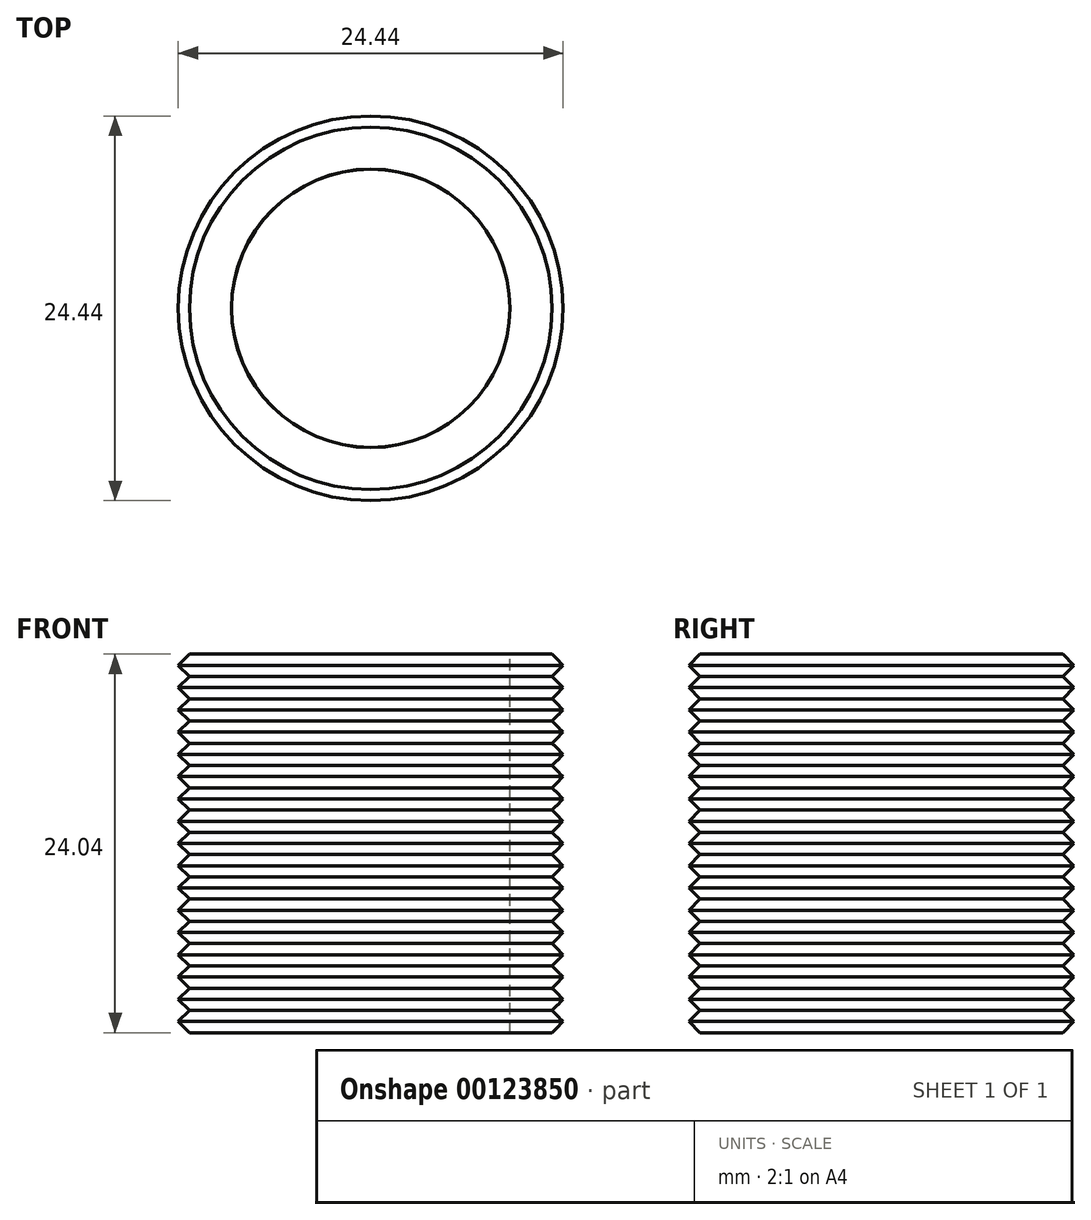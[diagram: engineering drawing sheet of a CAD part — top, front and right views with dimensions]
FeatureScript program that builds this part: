
annotation { "Feature Type Name" : "Feature", "Feature Type Description" : "" }
export const myFeature = defineFeature(function(context is Context, id is Id, definition is map)
    precondition{}
    {
        {
            var Q0;
            Q0=qCreatedBy(makeId("Front.planeOp"),FACE);
            var sketch = newSketch(context, id + "F0", { "sketchPlane" : qUnion([Q0])});
            skLineSegment(sketch, "E0.bottom", {"start": v(-8.84, 0) * mm, "end": v(-11.51, 0) * mm});
            skLineSegment(sketch, "E0.left", {"start": v(-8.84, 0) * mm, "end": v(-8.84, -24.04) * mm});
            skLineSegment(sketch, "E1", {"start": v(-11.51, 0) * mm, "end": v(-12.22, -0.7) * mm});
            skLineSegment(sketch, "E2", {"start": v(-12.22, -0.7) * mm, "end": v(-11.51, -1.41) * mm});
            skLineSegment(sketch, "E3", {"start": v(-11.51, -1.41) * mm, "end": v(-12.22, -2.12) * mm});
            skLineSegment(sketch, "E4", {"start": v(-12.22, -2.12) * mm, "end": v(-11.51, -2.83) * mm});
            skLineSegment(sketch, "E5", {"start": v(-11.51, -2.83) * mm, "end": v(-12.22, -3.54) * mm});
            skLineSegment(sketch, "E6", {"start": v(-12.22, -3.54) * mm, "end": v(-11.51, -4.24) * mm});
            skLineSegment(sketch, "E7", {"start": v(-11.51, -4.24) * mm, "end": v(-12.22, -4.95) * mm});
            skLineSegment(sketch, "E8", {"start": v(-12.22, -4.95) * mm, "end": v(-11.51, -5.66) * mm});
            skLineSegment(sketch, "E9", {"start": v(-11.51, -5.66) * mm, "end": v(-12.22, -6.36) * mm});
            skLineSegment(sketch, "E10", {"start": v(-12.22, -6.36) * mm, "end": v(-11.51, -7.07) * mm});
            skLineSegment(sketch, "E11", {"start": v(-11.51, -7.07) * mm, "end": v(-12.22, -7.78) * mm});
            skLineSegment(sketch, "E12", {"start": v(-12.22, -7.78) * mm, "end": v(-11.51, -8.49) * mm});
            skLineSegment(sketch, "E13", {"start": v(-11.51, -8.49) * mm, "end": v(-12.22, -9.2) * mm});
            skLineSegment(sketch, "E14", {"start": v(-12.22, -9.2) * mm, "end": v(-11.51, -9.9) * mm});
            skLineSegment(sketch, "E15", {"start": v(-11.51, -9.9) * mm, "end": v(-12.22, -10.6) * mm});
            skLineSegment(sketch, "E16", {"start": v(-12.22, -10.6) * mm, "end": v(-11.51, -11.31) * mm});
            skLineSegment(sketch, "E17", {"start": v(-11.51, -11.31) * mm, "end": v(-12.22, -12.02) * mm});
            skLineSegment(sketch, "E18", {"start": v(-12.22, -12.02) * mm, "end": v(-11.51, -12.73) * mm});
            skLineSegment(sketch, "E19", {"start": v(-11.51, -12.73) * mm, "end": v(-12.22, -13.44) * mm});
            skLineSegment(sketch, "E20", {"start": v(-12.22, -13.44) * mm, "end": v(-11.51, -14.14) * mm});
            skLineSegment(sketch, "E21", {"start": v(-11.51, -14.14) * mm, "end": v(-12.22, -14.85) * mm});
            skLineSegment(sketch, "E22", {"start": v(-12.22, -14.85) * mm, "end": v(-11.51, -15.56) * mm});
            skLineSegment(sketch, "E23", {"start": v(-11.51, -15.56) * mm, "end": v(-12.22, -16.26) * mm});
            skLineSegment(sketch, "E24", {"start": v(-12.22, -16.26) * mm, "end": v(-11.51, -16.97) * mm});
            skLineSegment(sketch, "E25", {"start": v(-11.51, -16.97) * mm, "end": v(-12.22, -17.68) * mm});
            skLineSegment(sketch, "E26", {"start": v(-12.22, -17.68) * mm, "end": v(-11.51, -18.38) * mm});
            skLineSegment(sketch, "E27", {"start": v(-11.51, -18.38) * mm, "end": v(-12.22, -19.1) * mm});
            skLineSegment(sketch, "E28", {"start": v(-12.22, -19.1) * mm, "end": v(-11.51, -19.8) * mm});
            skLineSegment(sketch, "E29", {"start": v(-11.51, -19.8) * mm, "end": v(-12.22, -20.5) * mm});
            skLineSegment(sketch, "E30", {"start": v(-12.22, -20.5) * mm, "end": v(-11.51, -21.21) * mm});
            skLineSegment(sketch, "E31", {"start": v(-11.51, -21.21) * mm, "end": v(-12.22, -21.92) * mm});
            skLineSegment(sketch, "E32", {"start": v(-12.22, -21.92) * mm, "end": v(-11.51, -22.63) * mm});
            skLineSegment(sketch, "E33", {"start": v(-11.51, -22.63) * mm, "end": v(-12.22, -23.33) * mm});
            skLineSegment(sketch, "E34", {"start": v(-12.22, -23.33) * mm, "end": v(-11.51, -24.04) * mm});
            skLineSegment(sketch, "E35", {"start": v(-11.51, -24.04) * mm, "end": v(-8.84, -24.04) * mm});
            skLineSegment(sketch, "E36", {"start": v(0, 0) * mm, "end": v(0, -19.97) * mm, "construction": true});
            skSolve(sketch);
        }
        {
            var Q0;
            Q0=makeQuery(id+"F0.imprint","IMPRINT",FACE,{"disambiguationData":[TD([[makeQuery(id+"F0.imprint","IMPRINT",EDGE,{"derivedFrom":sQuery(id+"F0.wireOp",EDGE,"E0.bottom")}),1.0]])]});
            var Q1;
            Q1=sQuery(id+"F0.wireOp",EDGE,"E36");
            revolve(context, id + "F1", {"entities" : qUnion([Q0]), "axis" : qUnion([Q1]), "revolveType" : RevolveType.FULL});
        }
    });
